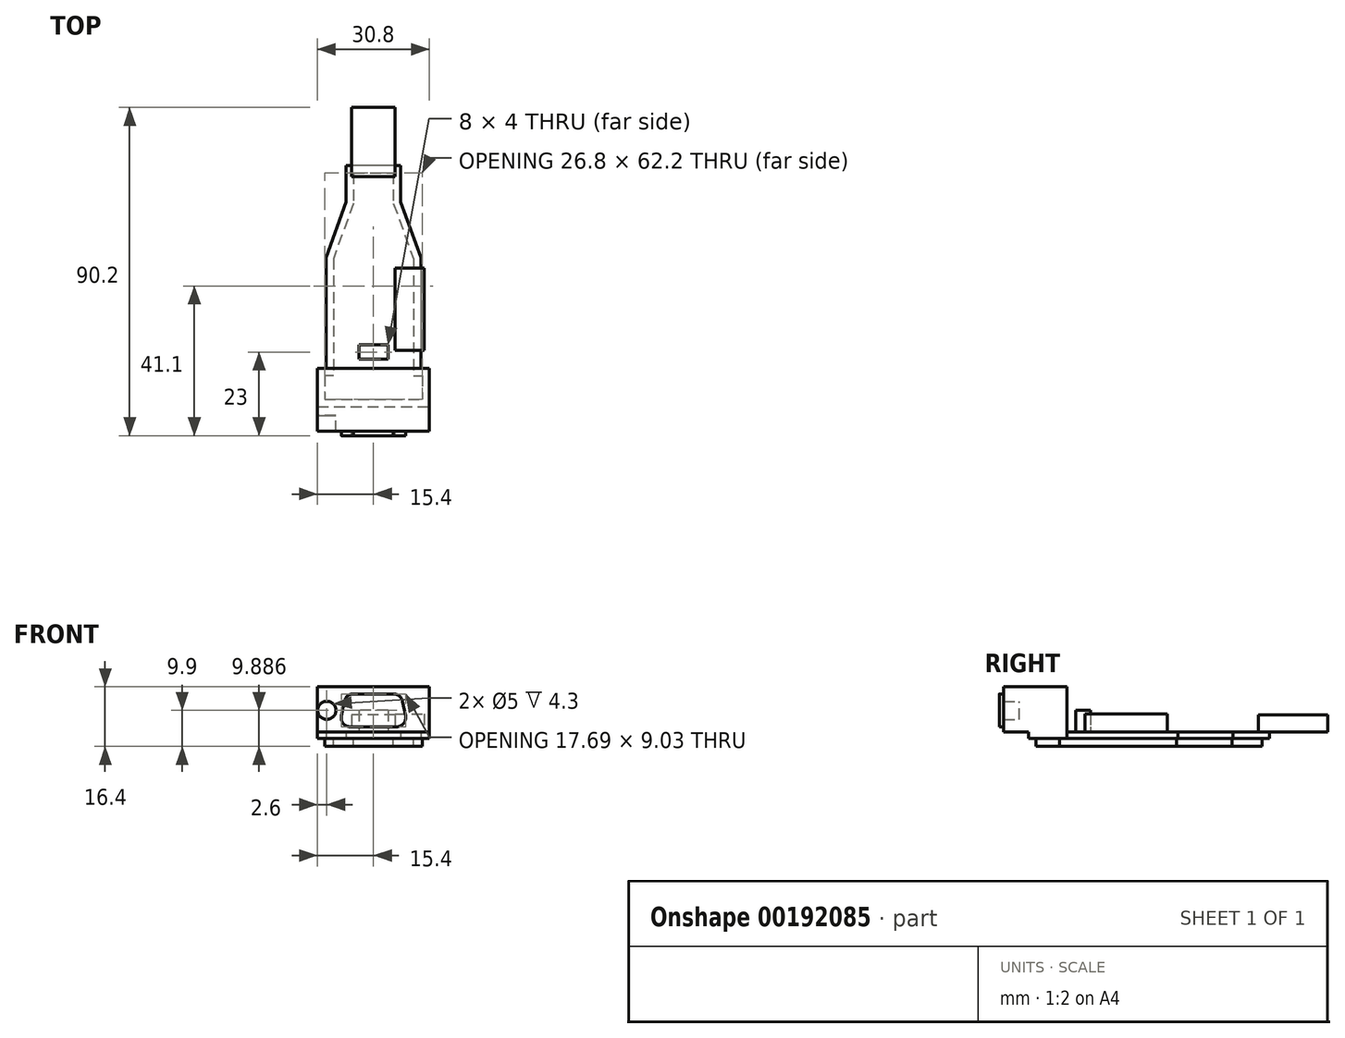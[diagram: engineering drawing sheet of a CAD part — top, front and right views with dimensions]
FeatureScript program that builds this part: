
annotation { "Feature Type Name" : "Feature", "Feature Type Description" : "" }
export const myFeature = defineFeature(function(context is Context, id is Id, definition is map)
    precondition{}
    {
        {
            var Q0;
            Q0=qCreatedBy(makeId("Top.planeOp"),FACE);
            var sketch = newSketch(context, id + "F0", { "sketchPlane" : qUnion([Q0])});
            skLineSegment(sketch, "E0", {"start": v(0, 25.2) * mm, "end": v(-7.5, 25.2) * mm});
            skLineSegment(sketch, "E1", {"start": v(-7.5, 25.2) * mm, "end": v(-7.5, 15.2) * mm});
            skLineSegment(sketch, "E2", {"start": v(-7.5, 15.2) * mm, "end": v(-13, 0) * mm});
            skLineSegment(sketch, "E3", {"start": v(-13, 0) * mm, "end": v(-13, -30.5) * mm});
            skLineSegment(sketch, "E4", {"start": v(-13, -30.5) * mm, "end": v(-15.4, -30.5) * mm});
            skLineSegment(sketch, "E5", {"start": v(-15.4, -30.5) * mm, "end": v(-15.4, -41) * mm});
            skLineSegment(sketch, "E6", {"start": v(-15.4, -41) * mm, "end": v(0, -41) * mm});
            skLineSegment(sketch, "E7.MirrorCS", {"start": v(15.4, -41) * mm, "end": v(0, -41) * mm});
            skLineSegment(sketch, "E8.MirrorCS", {"start": v(15.4, -30.5) * mm, "end": v(15.4, -41) * mm});
            skLineSegment(sketch, "E9.MirrorCS", {"start": v(13, -30.5) * mm, "end": v(15.4, -30.5) * mm});
            skLineSegment(sketch, "E10.MirrorCS", {"start": v(7.5, 15.2) * mm, "end": v(13, 0) * mm});
            skLineSegment(sketch, "E11.MirrorCS", {"start": v(0, 25.2) * mm, "end": v(7.5, 25.2) * mm});
            skLineSegment(sketch, "E12.MirrorCS", {"start": v(13, 0) * mm, "end": v(13, -30.5) * mm});
            skLineSegment(sketch, "E13.MirrorCS", {"start": v(7.5, 25.2) * mm, "end": v(7.5, 15.2) * mm});
            skSolve(sketch);
        }
        {
            var Q0;
            Q0=makeQuery(id+"F0.imprint","IMPRINT",FACE,{"disambiguationData":[TD([[makeQuery(id+"F0.imprint","IMPRINT",EDGE,{"derivedFrom":sQuery(id+"F0.wireOp",EDGE,"E0")}),1.0]])]});
            extrude(context, id + "F1", {"entities" : qUnion([Q0]), "depth" : 1.7 * mm});
        }
        {
            var Q0;
            Q0=makeQuery(id+"F1.opExtrude","CAP_FACE",FACE,{"disambiguationData":[OSD([sQuery(id+"F0.wireOp",EDGE,"E0"),sQuery(id+"F0.wireOp",EDGE,"E1"),sQuery(id+"F0.wireOp",EDGE,"E2"),sQuery(id+"F0.wireOp",EDGE,"E3"),sQuery(id+"F0.wireOp",EDGE,"E4"),sQuery(id+"F0.wireOp",EDGE,"E5"),sQuery(id+"F0.wireOp",EDGE,"E6"),sQuery(id+"F0.wireOp",EDGE,"E7.MirrorCS"),sQuery(id+"F0.wireOp",EDGE,"E8.MirrorCS"),sQuery(id+"F0.wireOp",EDGE,"E9.MirrorCS"),sQuery(id+"F0.wireOp",EDGE,"E10.MirrorCS"),sQuery(id+"F0.wireOp",EDGE,"E11.MirrorCS"),sQuery(id+"F0.wireOp",EDGE,"E12.MirrorCS"),sQuery(id+"F0.wireOp",EDGE,"E13.MirrorCS")])],"isStart":false});
            var sketch = newSketch(context, id + "F2", { "sketchPlane" : qUnion([Q0])});
            skLineSegment(sketch, "E14.bottom", {"start": v(6, 41.2) * mm, "end": v(-6, 41.2) * mm});
            skLineSegment(sketch, "E14.top", {"start": v(6, 22.2) * mm, "end": v(-6, 22.2) * mm});
            skLineSegment(sketch, "E14.left", {"start": v(6, 41.2) * mm, "end": v(6, 22.2) * mm});
            skLineSegment(sketch, "E14.right", {"start": v(-6, 41.2) * mm, "end": v(-6, 22.2) * mm});
            skSolve(sketch);
        }
        {
            var Q0;
            Q0 = qSketchRegion(id + "F2", true);
            extrude(context, id + "F3", {"entities" : qUnion([Q0]), "operationType" : NewBodyOperationType.ADD, "depth" : (6.5 - 1.7) * mm});
        }
        {
            var Q0;
            Q0=makeQuery(id+"F1.opExtrude","CAP_FACE",FACE,{"disambiguationData":[OSD([sQuery(id+"F0.wireOp",EDGE,"E0"),sQuery(id+"F0.wireOp",EDGE,"E1"),sQuery(id+"F0.wireOp",EDGE,"E2"),sQuery(id+"F0.wireOp",EDGE,"E3"),sQuery(id+"F0.wireOp",EDGE,"E4"),sQuery(id+"F0.wireOp",EDGE,"E5"),sQuery(id+"F0.wireOp",EDGE,"E6"),sQuery(id+"F0.wireOp",EDGE,"E7.MirrorCS"),sQuery(id+"F0.wireOp",EDGE,"E8.MirrorCS"),sQuery(id+"F0.wireOp",EDGE,"E9.MirrorCS"),sQuery(id+"F0.wireOp",EDGE,"E10.MirrorCS"),sQuery(id+"F0.wireOp",EDGE,"E11.MirrorCS"),sQuery(id+"F0.wireOp",EDGE,"E12.MirrorCS"),sQuery(id+"F0.wireOp",EDGE,"E13.MirrorCS")])],"isStart":false});
            var sketch = newSketch(context, id + "F4", { "sketchPlane" : qUnion([Q0])});
            skLineSegment(sketch, "E15.bottom", {"start": v(15.4, -30.5) * mm, "end": v(-15.4, -30.5) * mm});
            skLineSegment(sketch, "E15.top", {"start": v(15.4, -43.5) * mm, "end": v(-15.4, -43.5) * mm});
            skLineSegment(sketch, "E15.left", {"start": v(15.4, -30.5) * mm, "end": v(15.4, -43.5) * mm});
            skLineSegment(sketch, "E15.right", {"start": v(-15.4, -30.5) * mm, "end": v(-15.4, -43.5) * mm});
            skSolve(sketch);
        }
        {
            var Q0;
            Q0 = qSketchRegion(id + "F4", true);
            extrude(context, id + "F5", {"entities" : qUnion([Q0]), "operationType" : NewBodyOperationType.ADD, "depth" : 12.5 * mm});
        }
        {
            var Q0;
            Q0=makeQuery(id+"F5.opExtrude","SWEPT_FACE",FACE,{"disambiguationData":[OSD([sQuery(id+"F4.wireOp",EDGE,"E15.top")])]});
            var sketch = newSketch(context, id + "F6", { "sketchPlane" : qUnion([Q0])});
            skLineSegment(sketch, "E16", {"start": v(-8, 10.19) * mm, "end": v(-8.8, 6.15) * mm});
            skLineSegment(sketch, "E17.MirrorCS", {"start": v(8, 10.19) * mm, "end": v(8.8, 6.15) * mm});
            skPoint(sketch, "E18.visualSharp", {"position": v(-9.27, 3.8) * mm});
            skArc(sketch, "E18.filletArc", {"start": v(-8.8, 6.15) * mm, "mid": v(-8.14, 3.92) * mm, "end": v(-5.93, 3.2) * mm});
            skPoint(sketch, "E19.visualSharp", {"position": v(-7.48, 12.8) * mm});
            skArc(sketch, "E19.filletArc", {"start": v(-5.45, 12.2) * mm, "mid": v(-7.1, 11.67) * mm, "end": v(-8, 10.19) * mm});
            skPoint(sketch, "E20.visualSharp", {"position": v(9.27, 3.8) * mm});
            skArc(sketch, "E20.filletArc", {"start": v(5.93, 3.2) * mm, "mid": v(8.14, 3.92) * mm, "end": v(8.8, 6.15) * mm});
            skPoint(sketch, "E21.visualSharp", {"position": v(7.48, 12.8) * mm});
            skArc(sketch, "E21.filletArc", {"start": v(8, 10.19) * mm, "mid": v(7.1, 11.67) * mm, "end": v(5.45, 12.2) * mm});
            skCircle(sketch, "E22", {"center": v(12.8, 7.7) * mm, "radius": 2.5 * mm});
            skCircle(sketch, "E23.MirrorC", {"center": v(-12.8, 7.7) * mm, "radius": 2.5 * mm});
            skLineSegment(sketch, "E24", {"start": v(-5.45, 12.2) * mm, "end": v(5.45, 12.2) * mm});
            skLineSegment(sketch, "E25", {"start": v(-5.93, 3.2) * mm, "end": v(5.93, 3.2) * mm});
            skSolve(sketch);
        }
        {
            var Q0;
            Q0=makeQuery(id+"F6.imprint","IMPRINT",FACE,{"disambiguationData":[TD([[makeQuery(id+"F6.imprint","IMPRINT",EDGE,{"derivedFrom":sQuery(id+"F6.wireOp",EDGE,"E16")}),1.0]])]});
            extrude(context, id + "F7", {"entities" : qUnion([Q0]), "operationType" : NewBodyOperationType.ADD, "depth" : 5.5 * mm});
        }
        {
            var Q0;
            Q0=makeQuery(id+"F6.imprint","IMPRINT",FACE,{"disambiguationData":[TD([[makeQuery(id+"F6.imprint","IMPRINT",EDGE,{"derivedFrom":sQuery(id+"F6.wireOp",EDGE,"E23.MirrorC")}),-1.0]])]});
            var Q1;
            Q1=makeQuery(id+"F6.imprint","IMPRINT",FACE,{"disambiguationData":[TD([[makeQuery(id+"F6.imprint","IMPRINT",EDGE,{"derivedFrom":sQuery(id+"F6.wireOp",EDGE,"E22")}),1.0]])]});
            extrude(context, id + "F8", {"entities" : qUnion([Q0, Q1]), "operationType" : NewBodyOperationType.ADD, "depth" : 4.3 * mm});
        }
        {
            var Q0;
            Q0=makeQuery(id+"F1.opExtrude","CAP_FACE",FACE,{"disambiguationData":[OSD([sQuery(id+"F0.wireOp",EDGE,"E0"),sQuery(id+"F0.wireOp",EDGE,"E1"),sQuery(id+"F0.wireOp",EDGE,"E2"),sQuery(id+"F0.wireOp",EDGE,"E3"),sQuery(id+"F0.wireOp",EDGE,"E4"),sQuery(id+"F0.wireOp",EDGE,"E5"),sQuery(id+"F0.wireOp",EDGE,"E6"),sQuery(id+"F0.wireOp",EDGE,"E7.MirrorCS"),sQuery(id+"F0.wireOp",EDGE,"E8.MirrorCS"),sQuery(id+"F0.wireOp",EDGE,"E9.MirrorCS"),sQuery(id+"F0.wireOp",EDGE,"E10.MirrorCS"),sQuery(id+"F0.wireOp",EDGE,"E11.MirrorCS"),sQuery(id+"F0.wireOp",EDGE,"E12.MirrorCS"),sQuery(id+"F0.wireOp",EDGE,"E13.MirrorCS")])],"isStart":false});
            var sketch = newSketch(context, id + "F9", { "sketchPlane" : qUnion([Q0])});
            skLineSegment(sketch, "E26.bottom", {"start": v(5.9, -25.5) * mm, "end": v(13.9, -25.5) * mm});
            skLineSegment(sketch, "E26.top", {"start": v(5.9, -2.9) * mm, "end": v(13.9, -2.9) * mm});
            skLineSegment(sketch, "E26.left", {"start": v(5.9, -25.5) * mm, "end": v(5.9, -2.9) * mm});
            skLineSegment(sketch, "E26.right", {"start": v(13.9, -25.5) * mm, "end": v(13.9, -2.9) * mm});
            skSolve(sketch);
        }
        {
            var Q0;
            Q0 = qSketchRegion(id + "F9", true);
            extrude(context, id + "F10", {"entities" : qUnion([Q0]), "operationType" : NewBodyOperationType.ADD, "depth" : 5 * mm});
        }
        {
            var Q0;
            Q0=makeQuery(id+"F1.opExtrude","CAP_FACE",FACE,{"disambiguationData":[OSD([sQuery(id+"F0.wireOp",EDGE,"E0"),sQuery(id+"F0.wireOp",EDGE,"E1"),sQuery(id+"F0.wireOp",EDGE,"E2"),sQuery(id+"F0.wireOp",EDGE,"E3"),sQuery(id+"F0.wireOp",EDGE,"E4"),sQuery(id+"F0.wireOp",EDGE,"E5"),sQuery(id+"F0.wireOp",EDGE,"E6"),sQuery(id+"F0.wireOp",EDGE,"E7.MirrorCS"),sQuery(id+"F0.wireOp",EDGE,"E8.MirrorCS"),sQuery(id+"F0.wireOp",EDGE,"E9.MirrorCS"),sQuery(id+"F0.wireOp",EDGE,"E10.MirrorCS"),sQuery(id+"F0.wireOp",EDGE,"E11.MirrorCS"),sQuery(id+"F0.wireOp",EDGE,"E12.MirrorCS"),sQuery(id+"F0.wireOp",EDGE,"E13.MirrorCS")])],"isStart":true});
            var sketch = newSketch(context, id + "F11", { "sketchPlane" : qUnion([Q0])});
            skLineSegment(sketch, "E27.0", {"start": v(-5.5, -14.85) * mm, "end": v(-11, 0.35) * mm});
            skLineSegment(sketch, "E27.1", {"start": v(13.4, 32.5) * mm, "end": v(13.4, 39) * mm});
            skLineSegment(sketch, "E27.2", {"start": v(-13.4, 39) * mm, "end": v(13.4, 39) * mm});
            skLineSegment(sketch, "E27.3", {"start": v(-13.4, 32.5) * mm, "end": v(-13.4, 39) * mm});
            skLineSegment(sketch, "E27.4", {"start": v(-11, 32.5) * mm, "end": v(-13.4, 32.5) * mm});
            skLineSegment(sketch, "E27.5", {"start": v(11, 32.5) * mm, "end": v(13.4, 32.5) * mm});
            skLineSegment(sketch, "E27.6", {"start": v(-11, 0.35) * mm, "end": v(-11, 32.5) * mm});
            skLineSegment(sketch, "E27.7", {"start": v(11, 0.35) * mm, "end": v(11, 32.5) * mm});
            skLineSegment(sketch, "E27.8", {"start": v(5.5, -14.85) * mm, "end": v(11, 0.35) * mm});
            skLineSegment(sketch, "E27.9", {"start": v(5.5, -23.2) * mm, "end": v(5.5, -14.85) * mm});
            skLineSegment(sketch, "E27.10", {"start": v(-5.5, -23.2) * mm, "end": v(5.5, -23.2) * mm});
            skLineSegment(sketch, "E27.11", {"start": v(-5.5, -23.2) * mm, "end": v(-5.5, -14.85) * mm});
            skSolve(sketch);
        }
        {
            var Q0;
            Q0 = qSketchRegion(id + "F11", true);
            extrude(context, id + "F12", {"entities" : qUnion([Q0]), "operationType" : NewBodyOperationType.ADD, "depth" : 2.2 * mm});
        }
        {
            var Q0;
            Q0=makeQuery(id+"F1.opExtrude","CAP_FACE",FACE,{"disambiguationData":[OSD([sQuery(id+"F0.wireOp",EDGE,"E0"),sQuery(id+"F0.wireOp",EDGE,"E1"),sQuery(id+"F0.wireOp",EDGE,"E2"),sQuery(id+"F0.wireOp",EDGE,"E3"),sQuery(id+"F0.wireOp",EDGE,"E4"),sQuery(id+"F0.wireOp",EDGE,"E5"),sQuery(id+"F0.wireOp",EDGE,"E6"),sQuery(id+"F0.wireOp",EDGE,"E7.MirrorCS"),sQuery(id+"F0.wireOp",EDGE,"E8.MirrorCS"),sQuery(id+"F0.wireOp",EDGE,"E9.MirrorCS"),sQuery(id+"F0.wireOp",EDGE,"E10.MirrorCS"),sQuery(id+"F0.wireOp",EDGE,"E11.MirrorCS"),sQuery(id+"F0.wireOp",EDGE,"E12.MirrorCS"),sQuery(id+"F0.wireOp",EDGE,"E13.MirrorCS")])],"isStart":false});
            var sketch = newSketch(context, id + "F13", { "sketchPlane" : qUnion([Q0])});
            skLineSegment(sketch, "E28.bottom", {"start": v(4, -24) * mm, "end": v(-4, -24) * mm});
            skLineSegment(sketch, "E28.top", {"start": v(4, -28) * mm, "end": v(-4, -28) * mm});
            skLineSegment(sketch, "E28.left", {"start": v(4, -24) * mm, "end": v(4, -28) * mm});
            skLineSegment(sketch, "E28.right", {"start": v(-4, -24) * mm, "end": v(-4, -28) * mm});
            skSolve(sketch);
        }
        {
            var Q0;
            Q0 = qSketchRegion(id + "F13", true);
            extrude(context, id + "F14", {"entities" : qUnion([Q0]), "operationType" : NewBodyOperationType.ADD, "depth" : 6 * mm});
        }
        {
            var Q0;
            Q0=qCreatedBy(makeId("Top.planeOp"),FACE);
            var sketch = newSketch(context, id + "F15", { "sketchPlane" : qUnion([Q0])});
            skLineSegment(sketch, "E29.bottom", {"start": v(36.4, -30.5) * mm, "end": v(-49.42, -30.5) * mm});
            skLineSegment(sketch, "E29.top", {"start": v(36.4, -70.34) * mm, "end": v(-49.42, -70.34) * mm});
            skLineSegment(sketch, "E29.left", {"start": v(36.4, -30.5) * mm, "end": v(36.4, -70.34) * mm});
            skLineSegment(sketch, "E29.right", {"start": v(-49.42, -30.5) * mm, "end": v(-49.42, -70.34) * mm});
            skSolve(sketch);
        }
        {
            var Q0;
            Q0=makeQuery(id+"F1.opExtrude","SWEPT_BODY",BODY,{"disambiguationData":[OSD([sQuery(id+"F0.wireOp",EDGE,"E0"),sQuery(id+"F0.wireOp",EDGE,"E1"),sQuery(id+"F0.wireOp",EDGE,"E2"),sQuery(id+"F0.wireOp",EDGE,"E3"),sQuery(id+"F0.wireOp",EDGE,"E4"),sQuery(id+"F0.wireOp",EDGE,"E5"),sQuery(id+"F0.wireOp",EDGE,"E6"),sQuery(id+"F0.wireOp",EDGE,"E7.MirrorCS"),sQuery(id+"F0.wireOp",EDGE,"E8.MirrorCS"),sQuery(id+"F0.wireOp",EDGE,"E9.MirrorCS"),sQuery(id+"F0.wireOp",EDGE,"E10.MirrorCS"),sQuery(id+"F0.wireOp",EDGE,"E11.MirrorCS"),sQuery(id+"F0.wireOp",EDGE,"E12.MirrorCS"),sQuery(id+"F0.wireOp",EDGE,"E13.MirrorCS")])]});
            transform(context, id + "F16", {"entities" : qUnion([Q0]), "transformType" : TransformType.TRANSLATION_3D, "dx" : 0 * mm, "dy" : 0 * mm, "dz" : 0 * mm, "makeCopy" : true});
        }
    });
